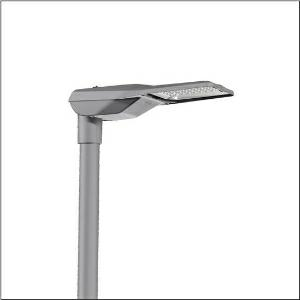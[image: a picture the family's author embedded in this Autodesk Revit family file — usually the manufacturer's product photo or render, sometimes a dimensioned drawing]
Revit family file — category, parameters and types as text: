
# Revit family: streetlight_sl_21_mini___p1_0a_5xe2a33s08hb_2caa
name_source: partatom
category: Lighting Fixtures
units: mm (PartAtom-declared; Revit-internal decimal feet)

## family parameters
Cut with Voids When Loaded = No
Host = Face
Light Source = No
Part Type = Normal
Room Calculation Point = No
Round Connector Dimension = Use Diameter
Shared = No

## types (1)
- --- (1 x LED, 9040 lm, 66 W, 3000K)
    Apparent Load = 66 VA
    CIE Flux Codes = 21 50 90 100 100
    Color Rendering = 70
    Color Temperature = 3000K
    Default Elevation = 1800 mm
    Description = Streetlight SL 21 mini, mast luminaire, primary light control with lens, of PMMA, primary optical cover: cover, of toughened safety glass, transparent, light distribution: P1.0a, light emission: direct distribution, primary light characteristic: asymmetric, installation type: side-entry, post-top, LED, High Power LED, rated luminous flux: 9.040lm, luminous efficacy: 137lm/W, light colour: 730, colour temperature: 3000K, control gear: D4i, control: overheat protection, constant luminous flux control, time-dependent luminous flux control, flexible luminous flux parameterisation, pre-setting: logarithmic dimming characteristic, mains connection: 220..240V, AC, 50/60Hz, start of lifetime: 66W, end of service life: 69W, reduction: 30W, luminaire housing, of diecast aluminium, powder-coated, Siteco® metallic grey (DB 702S), corrosivity category C5 mid according to DIN EN ISO 12944, please order mast flange separately, inclination adjustable: 0°, 5°, 10°, 15°, sealing non-destructively replaceable, multi-level sealing system, length: 628mm, width: 235mm, height: 110mm, mast flange for spigot size: 42mm (side-entry): 5XC10008XM4, 60/48mm (side-entry/post-top): 5XC10108XM2, 76/60mm (side-entry/post-top): 5XC10108XM1, mounting height: 4..8m, Smart Interface above, protection rating (complete): IP66, insulation class (complete): insulation class II (safety insulation), certification: CE, ENEC, ENEC+, VDE, impact resistance: IK10, permissible operating ambient temperature for outdoor applications: -40..+50°C, standard-compliant lighting for roads and squares, packaging unit: 1 piece

Light Distribution: P1.0a
    Height = 110 mm
    Lamp = 1 x LED
    Lamp Light Flux = 9040 lm
    Lamp Power = 66 W
    Lamp count = 1
    Length = 625 mm
    Luminous efficacy = 137 lm/W
    Manufacturer = Siteco
    ModVariant = No
    Model = 5XE2A33S08HB
    Number of Poles = 1
    OnlyDefault = Yes
    Power Factor = 1
    Product Name = Streetlight SL 21 mini | P1.0a
    Product group = mast luminaire | pylon top
    ProductGroupID = 6100
    Protection Class = Protection class II
    Protection Degree = IP 66
    RLX_Detail_Level = 1
    RLX_Emergency_Light_Flux = 0 lm
    RLX_Emergency_Type = 0
    RLX_Emergency_Type_DB = No
    RlxData = <blob elided: 37425 chars, md5=f0c381ec>
    Socket = socket
    Standby Power = 0 W
    System Light Flux = 9040 lm
    System Power = 66 W
    Type Comments = factory setting: luminous flux: 100 % | dim-lin: 254 | 670 mA
    Type Image = l_1003515.jpg
    URL = http://relux.com
    VarID = @adj_186626
    Voltage = 0 V
    Weight = 0.00 kg
    Width = 234 mm

## geometry (parser evidence)
native form markers: Blend x4, Sweep x11
no freeform markers — native parametric forms only
